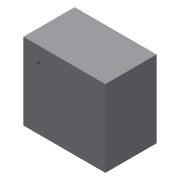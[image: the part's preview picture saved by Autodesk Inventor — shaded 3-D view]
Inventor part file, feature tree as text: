
AUTODESK INVENTOR PART (.ipt)
format: ipt  version: 2013 (Build 170138000, 138)  size: 190,976 bytes
history: native  units: mm
features: sketch x10, extrude x7, hole x4, fillet x3
ambient origin geometry x8: Origin, YZ Plane, XZ Plane, XY Plane, X Axis, Y Axis, Z Axis, Center Point
bodies: Solid1 (feature_tree)
feature tree (24):
  extrude  "Extrusion1"  Depth=46.0mm TaperAngle=0.0deg
  extrude  "Extrusion2"  Depth=60.0mm
  extrude  "Extrusion3"  Depth=15.0mm
  extrude  "Extrusion4"  Depth=5.0mm
  extrude  "Extrusion5"  Depth=30.0mm
  fillet  "Fillet7"  Radius=42.0mm
  fillet  "Fillet8"  Radius=30.0mm
  hole  "Hole1"  [1 undecoded]
  fillet  "Fillet9"  Radius=32.0mm
  extrude  "Extrusion12"  Depth=8.0mm TaperAngle=0.0deg
  hole  "Hole4"  [1 undecoded]
  extrude  "Extrusion13"  Depth=12.0mm
  hole  "Hole5"  [1 undecoded]
  hole  "Hole6"  [1 undecoded]
  sketch  "Sketch1"  dims[d0=50.0mm d1=0.0mm d2=46.0mm d3=0.0mm]
  sketch  "Sketch2"  dims[d4=60.0mm d7=60.0mm]
  sketch  "Sketch3"  dims[d8=15.0mm d9=15.0mm]
  sketch  "Sketch4"  dims[d10=3.0mm d11=5.0mm]
  sketch  "Sketch5"  dims[d12=25.0mm d13=30.0mm d14=42.0mm d15=30.0mm d16=0.0mm]
  sketch  "Sketch10"  dims[d17=25.0mm d18=30.0mm d19=32.0mm]
  sketch  "Sketch15"  dims[d20=30.0mm d21=0.0mm d34=8.0mm d35=0.0mm]
  sketch  "Sketch16"  dims[d61=20.0mm d62=2.0mm]
  sketch  "Sketch17"  dims[d71=7.0mm d72=12.0mm]
  sketch  "Sketch18"  dims[d73=6.4mm d74=6.0mm d75=4.0mm d76=2.0mm d77=90.0deg d78=30.0mm d79=20.594885mm d80=10.0mm d103=15.0mm d104=0.0mm d105=36.0mm d106=36.0mm d107=2.156mm d108=6.0mm d109=4.0mm d110=2.0mm d111=90.0deg d112=8.0mm d113=20.594885mm d114=20.0mm d115=0.0mm d116=30.0mm d117=30.0mm d118=2.156mm d119=6.0mm d120=4.0mm d121=2.0mm d122=90.0deg d123=8.0mm d124=20.594885mm d125=15.0mm d126=15.0mm d127=3.302mm d128=6.0mm d129=4.0mm d130=2.0mm d131=90.0deg d132=8.0mm d133=20.594885mm]
note: 4 required parameter values undecoded (feature->parameter linkage not recoverable at this tier; creation-order binding heuristic only, values carry confidence <= 0.55)
